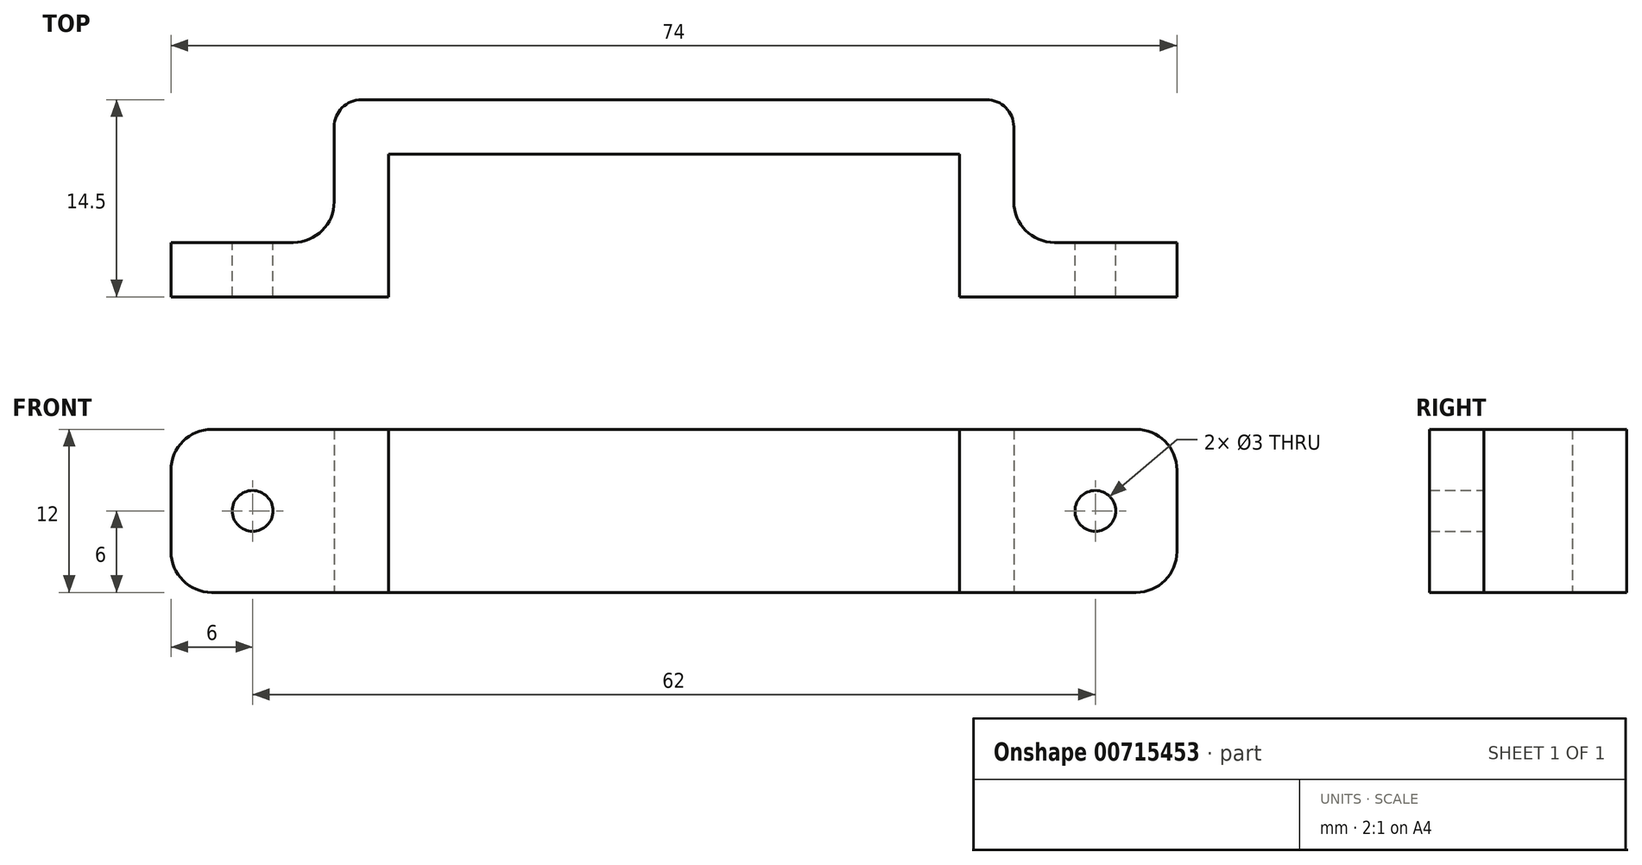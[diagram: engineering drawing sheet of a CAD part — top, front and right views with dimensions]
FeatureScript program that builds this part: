
annotation { "Feature Type Name" : "Feature", "Feature Type Description" : "" }
export const myFeature = defineFeature(function(context is Context, id is Id, definition is map)
    precondition{}
    {
        {
            var Q0;
            Q0=qCreatedBy(makeId("Top.planeOp"),FACE);
            var sketch = newSketch(context, id + "F0", { "sketchPlane" : qUnion([Q0])});
            skLineSegment(sketch, "E0", {"start": v(5.88, 2.16) * mm, "end": v(5.88, -1.84) * mm});
            skLineSegment(sketch, "E1", {"start": v(5.88, -1.84) * mm, "end": v(21.88, -1.84) * mm});
            skLineSegment(sketch, "E2", {"start": v(21.88, -1.84) * mm, "end": v(21.88, 8.66) * mm});
            skLineSegment(sketch, "E3", {"start": v(21.88, 8.66) * mm, "end": v(63.88, 8.66) * mm});
            skLineSegment(sketch, "E4", {"start": v(63.88, 8.66) * mm, "end": v(63.88, -1.84) * mm});
            skLineSegment(sketch, "E5", {"start": v(63.88, -1.84) * mm, "end": v(79.88, -1.84) * mm});
            skLineSegment(sketch, "E6", {"start": v(79.88, -1.84) * mm, "end": v(79.88, 2.16) * mm});
            skLineSegment(sketch, "E7", {"start": v(79.88, 2.16) * mm, "end": v(67.88, 2.16) * mm});
            skLineSegment(sketch, "E8", {"start": v(67.88, 2.16) * mm, "end": v(67.88, 12.66) * mm});
            skLineSegment(sketch, "E9", {"start": v(67.88, 12.66) * mm, "end": v(17.88, 12.66) * mm});
            skLineSegment(sketch, "E10", {"start": v(17.88, 12.66) * mm, "end": v(17.88, 2.16) * mm});
            skLineSegment(sketch, "E11", {"start": v(17.88, 2.16) * mm, "end": v(5.88, 2.16) * mm});
            skSolve(sketch);
        }
        {
            var Q0;
            Q0=makeQuery(id+"F0.imprint","IMPRINT",FACE,{"disambiguationData":[TD([[makeQuery(id+"F0.imprint","IMPRINT",EDGE,{"derivedFrom":sQuery(id+"F0.wireOp",EDGE,"E0")}),1.0]])]});
            extrude(context, id + "F1", {"entities" : qUnion([Q0]), "depth" : 12 * mm, "offsetDistance" : 25 * mm});
        }
        {
            var Q0;
            Q0=makeQuery(id+"F1.opExtrude","SWEPT_FACE",FACE,{"disambiguationData":[OSD([sQuery(id+"F0.wireOp",EDGE,"E1")])]});
            var sketch = newSketch(context, id + "F2", { "sketchPlane" : qUnion([Q0])});
            skPoint(sketch, "E12", {"position": v(11.88, 6) * mm});
            skPoint(sketch, "E12.positionSnap0", {"position": v(5.88, 6) * mm});
            skPoint(sketch, "E13", {"position": v(73.88, 6) * mm});
            skSolve(sketch);
        }
        {
            var Q0;
            Q0=sQuery(id+"F2.wireOp",VERTEX,"E12");
            var Q1;
            Q1=sQuery(id+"F2.wireOp",VERTEX,"E13");
            var Q2;
            Q2=makeQuery(id+"F1.opExtrude","SWEPT_BODY",BODY,{"disambiguationData":[OSD([sQuery(id+"F0.wireOp",EDGE,"E0"),sQuery(id+"F0.wireOp",EDGE,"E1"),sQuery(id+"F0.wireOp",EDGE,"E2"),sQuery(id+"F0.wireOp",EDGE,"E3"),sQuery(id+"F0.wireOp",EDGE,"E4"),sQuery(id+"F0.wireOp",EDGE,"E5"),sQuery(id+"F0.wireOp",EDGE,"E6"),sQuery(id+"F0.wireOp",EDGE,"E7"),sQuery(id+"F0.wireOp",EDGE,"E8"),sQuery(id+"F0.wireOp",EDGE,"E9"),sQuery(id+"F0.wireOp",EDGE,"E10"),sQuery(id+"F0.wireOp",EDGE,"E11")])]});
            hole(context, id + "F3", {"style" : HoleStyle.SIMPLE, "endStyle" : HoleEndStyle.BLIND, "holeDiameter" : 3 * mm, "majorDiameter" : 5 * mm, "holeDepth" : 25 * mm, "isTappedThrough" : true, "tappedDepth" : 12 * mm, "tapClearance" : 3, "locations" : qUnion([Q0, Q1]), "scope" : qUnion([Q2]), "startStyle" : HoleStartStyle.SKETCH});
        }
        {
            var Q0;
            Q0=makeQuery(id+"F1.opExtrude","SWEPT_EDGE",EDGE,{"disambiguationData":[OSD([sQuery(id+"F0.wireOp",EDGE,"E7"),sQuery(id+"F0.wireOp",EDGE,"E8")])]});
            var Q1;
            Q1=makeQuery(id+"F1.opExtrude","CAP_EDGE",EDGE,{"disambiguationData":[OSD([sQuery(id+"F0.wireOp",EDGE,"E6")])],"isStart":false});
            var Q2;
            Q2=makeQuery(id+"F1.opExtrude","CAP_EDGE",EDGE,{"disambiguationData":[OSD([sQuery(id+"F0.wireOp",EDGE,"E6")])],"isStart":true});
            var Q3;
            Q3=makeQuery(id+"F1.opExtrude","CAP_EDGE",EDGE,{"disambiguationData":[OSD([sQuery(id+"F0.wireOp",EDGE,"E0")])],"isStart":true});
            var Q4;
            Q4=makeQuery(id+"F1.opExtrude","SWEPT_EDGE",EDGE,{"disambiguationData":[OSD([sQuery(id+"F0.wireOp",EDGE,"E10"),sQuery(id+"F0.wireOp",EDGE,"E11")])]});
            var Q5;
            Q5=makeQuery(id+"F1.opExtrude","CAP_EDGE",EDGE,{"disambiguationData":[OSD([sQuery(id+"F0.wireOp",EDGE,"E0")])],"isStart":false});
            fillet(context, id + "F4", {"entities" : qUnion([Q0, Q1, Q2, Q3, Q4, Q5]), "tangentPropagation" : true, "radius" : 3 * mm, "defaultsChanged" : false, "vertexSettings" : [], "allowEdgeOverflow" : false});
        }
        {
            var Q0;
            Q0=makeQuery(id+"F1.opExtrude","SWEPT_EDGE",EDGE,{"disambiguationData":[OSD([sQuery(id+"F0.wireOp",EDGE,"E9"),sQuery(id+"F0.wireOp",EDGE,"E10")])]});
            var Q1;
            Q1=makeQuery(id+"F1.opExtrude","SWEPT_EDGE",EDGE,{"disambiguationData":[OSD([sQuery(id+"F0.wireOp",EDGE,"E8"),sQuery(id+"F0.wireOp",EDGE,"E9")])]});
            fillet(context, id + "F5", {"entities" : qUnion([Q0, Q1]), "tangentPropagation" : true, "radius" : 2 * mm, "defaultsChanged" : false, "vertexSettings" : [], "allowEdgeOverflow" : false});
        }
    });
